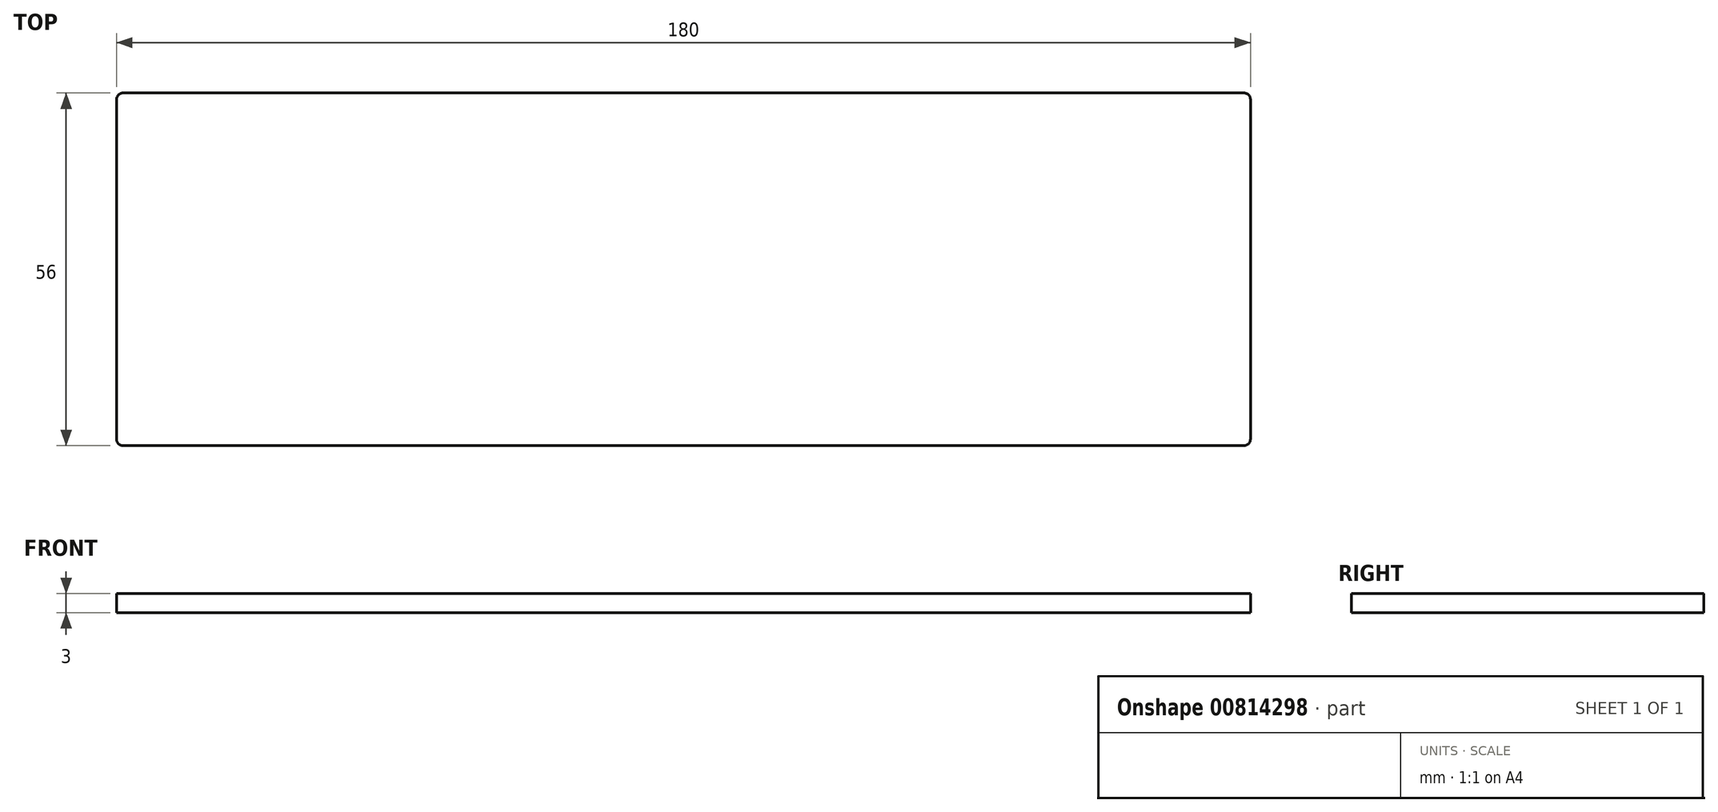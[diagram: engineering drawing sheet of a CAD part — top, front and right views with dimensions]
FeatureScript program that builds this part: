
annotation { "Feature Type Name" : "Feature", "Feature Type Description" : "" }
export const myFeature = defineFeature(function(context is Context, id is Id, definition is map)
    precondition{}
    {
        {
            var Q0;
            Q0=qCreatedBy(makeId("Top.planeOp"),FACE);
            var sketch = newSketch(context, id + "F0", { "sketchPlane" : qUnion([Q0])});
            skLineSegment(sketch, "E0.bottom", {"start": v(90, 28) * mm, "end": v(-90, 28) * mm});
            skLineSegment(sketch, "E0.top", {"start": v(90, -28) * mm, "end": v(-90, -28) * mm});
            skLineSegment(sketch, "E0.left", {"start": v(90, 28) * mm, "end": v(90, -28) * mm});
            skLineSegment(sketch, "E0.right", {"start": v(-90, 28) * mm, "end": v(-90, -28) * mm});
            skPoint(sketch, "E0.middle", {"position": v(0, 0) * mm});
            skSolve(sketch);
        }
        {
            var Q0;
            Q0 = qSketchRegion(id + "F0", true);
            extrude(context, id + "F1", {"entities" : qUnion([Q0]), "depth" : 3 * mm, "offsetDistance" : 25 * mm});
        }
        {
            var Q0;
            Q0=makeQuery(id+"F1.opExtrude","SWEPT_EDGE",EDGE,{"disambiguationData":[OSD([sQuery(id+"F0.wireOp",EDGE,"E0.top"),sQuery(id+"F0.wireOp",EDGE,"E0.right")])]});
            var Q1;
            Q1=makeQuery(id+"F1.opExtrude","SWEPT_EDGE",EDGE,{"disambiguationData":[OSD([sQuery(id+"F0.wireOp",EDGE,"E0.bottom"),sQuery(id+"F0.wireOp",EDGE,"E0.right")])]});
            var Q2;
            Q2=makeQuery(id+"F1.opExtrude","SWEPT_EDGE",EDGE,{"disambiguationData":[OSD([sQuery(id+"F0.wireOp",EDGE,"E0.bottom"),sQuery(id+"F0.wireOp",EDGE,"E0.left")])]});
            var Q3;
            Q3=makeQuery(id+"F1.opExtrude","SWEPT_EDGE",EDGE,{"disambiguationData":[OSD([sQuery(id+"F0.wireOp",EDGE,"E0.top"),sQuery(id+"F0.wireOp",EDGE,"E0.left")])]});
            fillet(context, id + "F2", {"entities" : qUnion([Q0, Q1, Q2, Q3]), "radius" : 1 * mm, "tangentPropagation" : true, "allowEdgeOverflow" : false});
        }
    });
